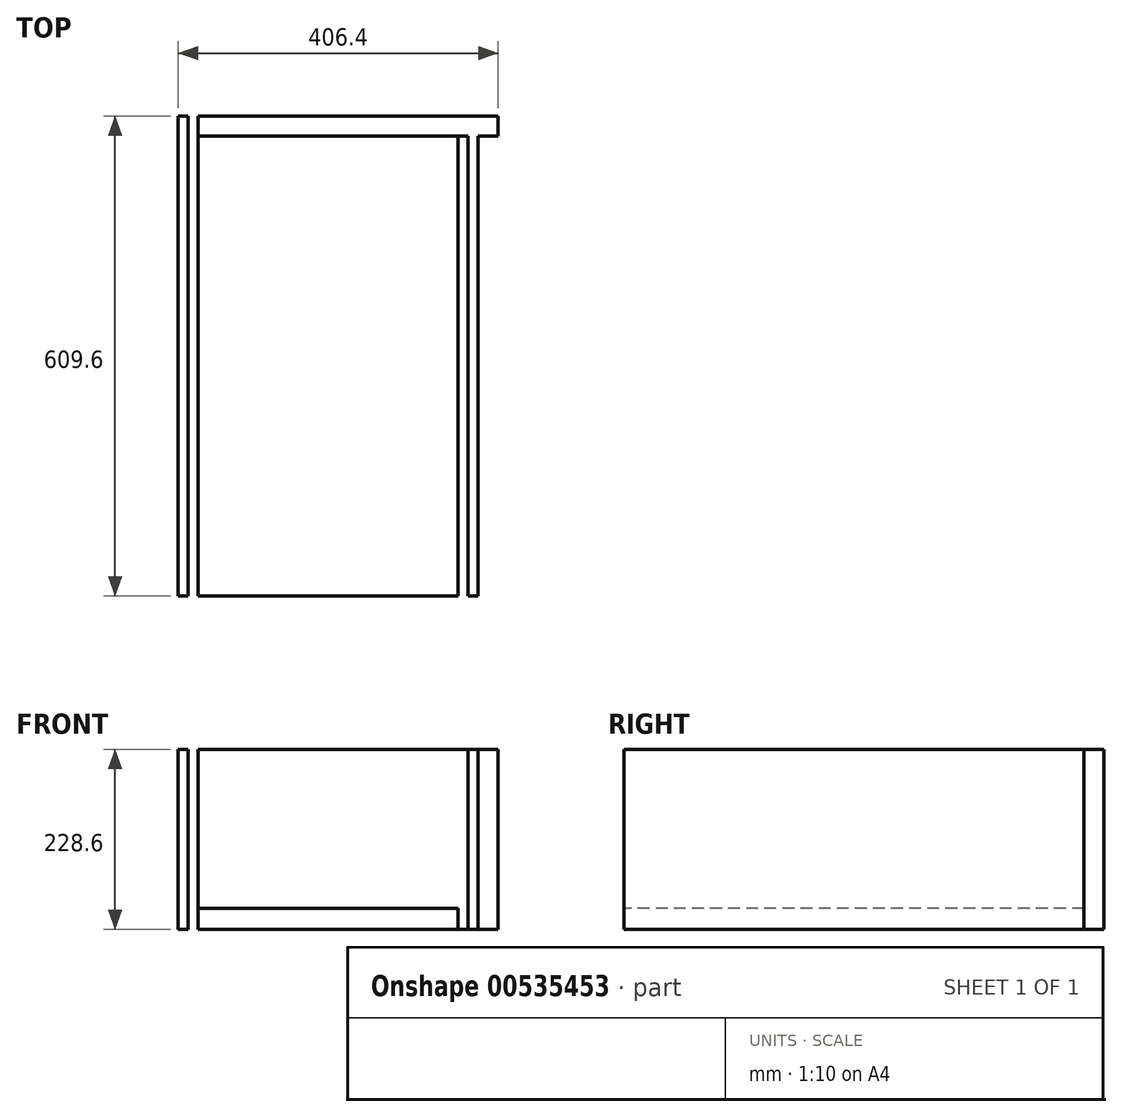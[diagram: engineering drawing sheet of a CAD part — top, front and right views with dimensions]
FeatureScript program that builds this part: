
annotation { "Feature Type Name" : "Feature", "Feature Type Description" : "" }
export const myFeature = defineFeature(function(context is Context, id is Id, definition is map)
    precondition{}
    {
        {
            var Q0;
            Q0=qCreatedBy(makeId("Front.planeOp"),FACE);
            var sketch = newSketch(context, id + "F0", { "sketchPlane" : qUnion([Q0])});
            skLineSegment(sketch, "E0.bottom", {"start": v(-190.5, 127) * mm, "end": v(190.5, 127) * mm});
            skLineSegment(sketch, "E0.top", {"start": v(-190.5, -127) * mm, "end": v(190.5, -127) * mm});
            skLineSegment(sketch, "E0.left", {"start": v(-190.5, 127) * mm, "end": v(-190.5, -127) * mm});
            skLineSegment(sketch, "E0.right", {"start": v(190.5, 127) * mm, "end": v(190.5, -127) * mm});
            skPoint(sketch, "E0.middle", {"position": v(0, 0) * mm});
            skLineSegment(sketch, "E1.left", {"start": v(-190.5, -127) * mm, "end": v(-190.5, -100.27) * mm});
            skLineSegment(sketch, "E1.right", {"start": v(190.5, -127) * mm, "end": v(190.5, -100.27) * mm});
            skLineSegment(sketch, "E2.bottom", {"start": v(-190.5, -127) * mm, "end": v(-165.1, -127) * mm});
            skLineSegment(sketch, "E2.top", {"start": v(-190.5, 101.6) * mm, "end": v(-165.1, 101.6) * mm});
            skLineSegment(sketch, "E2.left", {"start": v(-190.5, -127) * mm, "end": v(-190.5, 101.6) * mm});
            skLineSegment(sketch, "E2.right", {"start": v(-165.1, -127) * mm, "end": v(-165.1, 101.6) * mm});
            skLineSegment(sketch, "E3.bottom", {"start": v(190.5, -127) * mm, "end": v(165.1, -127) * mm});
            skLineSegment(sketch, "E3.top", {"start": v(190.5, 101.6) * mm, "end": v(165.1, 101.6) * mm});
            skLineSegment(sketch, "E3.left", {"start": v(190.5, -127) * mm, "end": v(190.5, 101.6) * mm});
            skLineSegment(sketch, "E3.right", {"start": v(165.1, -127) * mm, "end": v(165.1, 101.6) * mm});
            skLineSegment(sketch, "E4", {"start": v(-177.8, 101.6) * mm, "end": v(-177.8, -127) * mm});
            skLineSegment(sketch, "E5", {"start": v(177.8, 101.6) * mm, "end": v(177.8, -127) * mm});
            skLineSegment(sketch, "E6", {"start": v(-165.1, -100.59) * mm, "end": v(165.1, -100.59) * mm});
            skSolve(sketch);
        }
        {
            var Q0;
            {var subQ0=sQuery(id+"F0.wireOp",EDGE,"E4");var subQ1=sQuery(id+"F0.wireOp",EDGE,"E1.top");var subQ2=makeQuery(id+"F0.imprint","INTERSECT",VERTEX,{"derivedFrom":[subQ1,subQ0]});Q0=makeQuery(id+"F0.imprint","IMPRINT",FACE,{"disambiguationData":[TD([[makeQuery(id+"F0.imprint","IMPRINT",EDGE,{"disambiguationData":[TD([[subQ2,-1.0]])],"derivedFrom":subQ1}),1.0]])]});}
            var Q1;
            {var subQ0=sQuery(id+"F0.wireOp",EDGE,"E4");var subQ1=sQuery(id+"F0.wireOp",EDGE,"E1.top");var subQ2=makeQuery(id+"F0.imprint","INTERSECT",VERTEX,{"derivedFrom":[subQ1,subQ0]});Q1=makeQuery(id+"F0.imprint","IMPRINT",FACE,{"disambiguationData":[TD([[makeQuery(id+"F0.imprint","IMPRINT",EDGE,{"disambiguationData":[TD([[subQ2,-1.0]])],"derivedFrom":subQ1}),-1.0]])]});}
            var Q2;
            {var subQ0=sQuery(id+"F0.wireOp",EDGE,"E3.right");var subQ1=sQuery(id+"F0.wireOp",EDGE,"E1.top");var subQ2=makeQuery(id+"F0.imprint","INTERSECT",VERTEX,{"derivedFrom":[subQ1,subQ0]});Q2=makeQuery(id+"F0.imprint","IMPRINT",FACE,{"disambiguationData":[TD([[makeQuery(id+"F0.imprint","IMPRINT",EDGE,{"disambiguationData":[TD([[subQ2,-1.0]])],"derivedFrom":subQ1}),-1.0]])]});}
            var Q3;
            {var subQ0=sQuery(id+"F0.wireOp",EDGE,"E3.right");var subQ1=sQuery(id+"F0.wireOp",EDGE,"E1.top");var subQ2=makeQuery(id+"F0.imprint","INTERSECT",VERTEX,{"derivedFrom":[subQ1,subQ0]});Q3=makeQuery(id+"F0.imprint","IMPRINT",FACE,{"disambiguationData":[TD([[makeQuery(id+"F0.imprint","IMPRINT",EDGE,{"disambiguationData":[TD([[subQ2,-1.0]])],"derivedFrom":subQ1}),1.0]])]});}
            var Q4;
            {var subQ0=sQuery(id+"F0.wireOp",EDGE,"E0.top");Q4=makeQuery(id+"F0.imprint","IMPRINT",FACE,{"disambiguationData":[TD([[makeQuery(id+"F0.imprint","IMPRINT",EDGE,{"derivedFrom":subQ0}),1.0]])]});}
            extrude(context, id + "F1", {"entities" : qUnion([Q0, Q1, Q2, Q3, Q4]), "oppositeDirection" : true, "depth" : 609.6 * mm, "offsetDistance" : 25.4 * mm});
        }
        {
            var Q0;
            Q0=makeQuery(id+"F1.opExtrude","CAP_FACE",FACE,{"disambiguationData":[OSD([sQuery(id+"F0.wireOp",EDGE,"E0.top"),sQuery(id+"F0.wireOp",EDGE,"E1.top"),sQuery(id+"F0.wireOp",EDGE,"E2.bottom"),sQuery(id+"F0.wireOp",EDGE,"E2.top"),sQuery(id+"F0.wireOp",EDGE,"E2.left"),sQuery(id+"F0.wireOp",EDGE,"E2.right"),sQuery(id+"F0.wireOp",EDGE,"E3.bottom"),sQuery(id+"F0.wireOp",EDGE,"E3.top"),sQuery(id+"F0.wireOp",EDGE,"E3.left"),sQuery(id+"F0.wireOp",EDGE,"E3.right")])],"isStart":false});
            var sketch = newSketch(context, id + "F2", { "sketchPlane" : qUnion([Q0])});
            skLineSegment(sketch, "E7.bottom", {"start": v(-215.9, 101.6) * mm, "end": v(165.1, 101.6) * mm});
            skLineSegment(sketch, "E7.top", {"start": v(-215.9, -127) * mm, "end": v(165.1, -127) * mm});
            skLineSegment(sketch, "E7.left", {"start": v(-215.9, 101.6) * mm, "end": v(-215.9, -127) * mm});
            skLineSegment(sketch, "E7.right", {"start": v(165.1, 101.6) * mm, "end": v(165.1, -127) * mm});
            skSolve(sketch);
        }
        {
            var Q0;
            Q0 = qSketchRegion(id + "F2", true);
            extrude(context, id + "F3", {"entities" : qUnion([Q0]), "operationType" : NewBodyOperationType.ADD, "oppositeDirection" : true, "depth" : 25.4 * mm, "offsetDistance" : 25.4 * mm});
        }
    });
